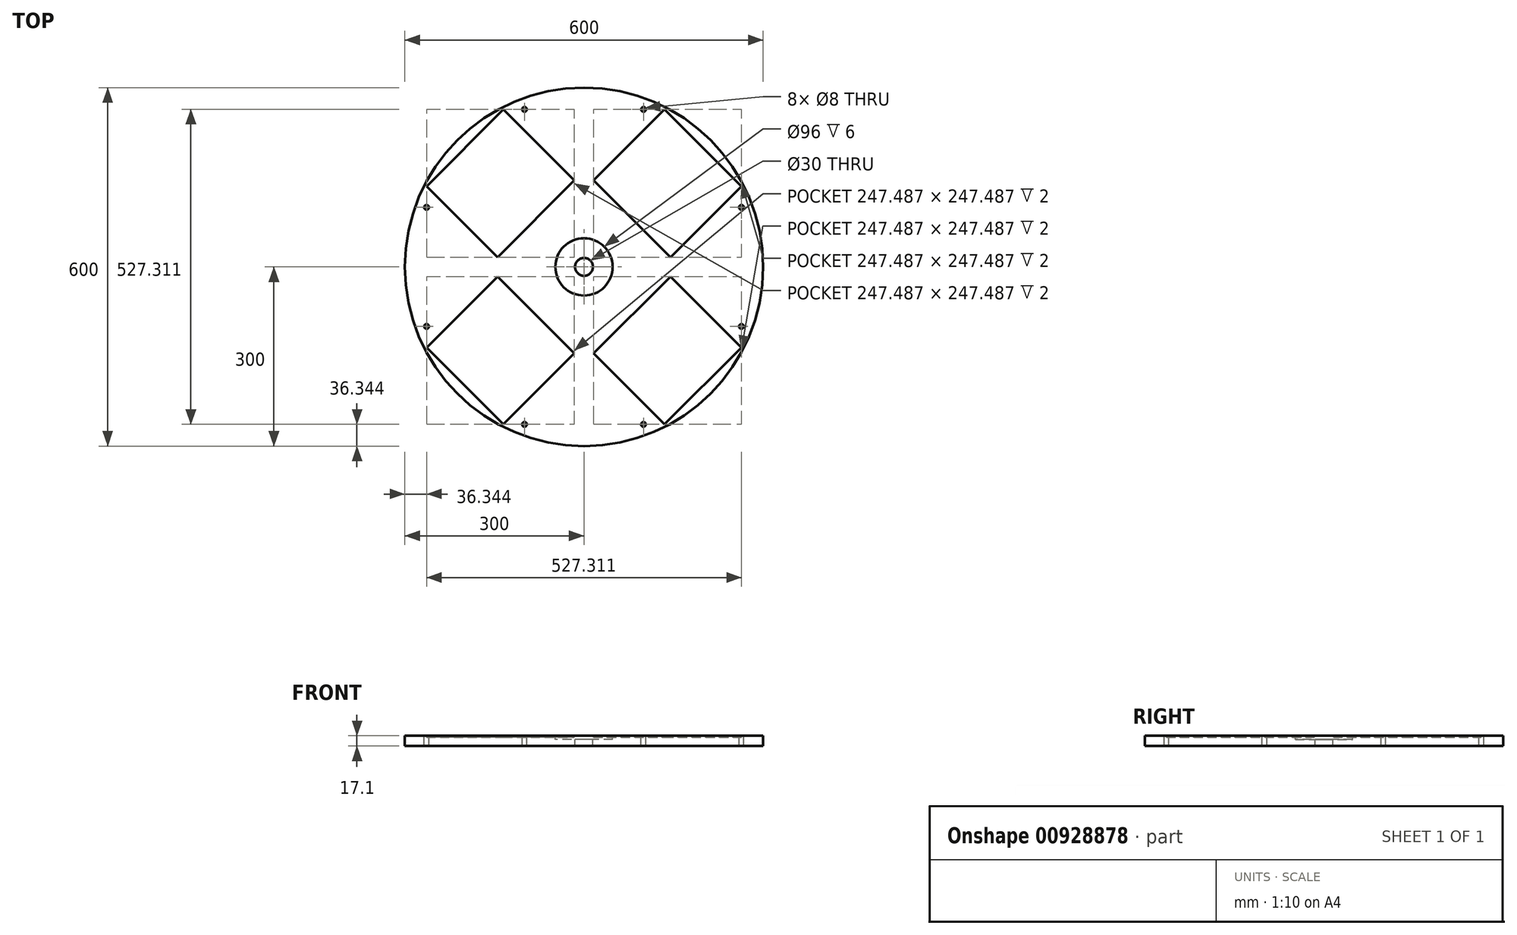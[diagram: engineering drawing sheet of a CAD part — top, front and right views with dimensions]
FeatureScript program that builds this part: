
annotation { "Feature Type Name" : "Feature", "Feature Type Description" : "" }
export const myFeature = defineFeature(function(context is Context, id is Id, definition is map)
    precondition{}
    {
        {
            var Q0;
            Q0=qCreatedBy(makeId("Top.planeOp"),FACE);
            var sketch = newSketch(context, id + "F0", { "sketchPlane" : qUnion([Q0])});
            skCircle(sketch, "E0", {"center": v(0, 0) * mm, "radius": 300 * mm});
            skSolve(sketch);
        }
        {
            var Q0;
            Q0=qSketchRegion(id+"F0",true);
            var Q1;
            Q1=makeQuery(id+"F0.imprint","IMPRINT",FACE,{"disambiguationData":[TD([[makeQuery(id+"F0.imprint","IMPRINT",EDGE,{"derivedFrom":sQuery(id+"F0.wireOp",EDGE,"AllwrVL7-AkE9-LfNM-VB61-ajPjN6t2vvd7.bottom")}),-1.0]])]});
            var Q2;
            Q2=makeQuery(id+"F0.imprint","IMPRINT",FACE,{"disambiguationData":[TD([[makeQuery(id+"F0.imprint","IMPRINT",EDGE,{"derivedFrom":sQuery(id+"F0.wireOp",EDGE,"5d97284d-aa32-4368-b48b-b87623f71f09.3.0")}),1.0]])]});
            var Q3;
            Q3=makeQuery(id+"F0.imprint","IMPRINT",FACE,{"disambiguationData":[TD([[makeQuery(id+"F0.imprint","IMPRINT",EDGE,{"derivedFrom":sQuery(id+"F0.wireOp",EDGE,"5d97284d-aa32-4368-b48b-b87623f71f09.2.0")}),1.0]])]});
            var Q4;
            Q4=makeQuery(id+"F0.imprint","IMPRINT",FACE,{"disambiguationData":[TD([[makeQuery(id+"F0.imprint","IMPRINT",EDGE,{"derivedFrom":sQuery(id+"F0.wireOp",EDGE,"5d97284d-aa32-4368-b48b-b87623f71f09.1.0")}),1.0]])]});
            extrude(context, id + "F1", {"entities" : qUnion([Q0, Q1, Q2, Q3, Q4]), "depth" : 17.1 * mm, "offsetDistance" : 25 * mm});
        }
        {
            var Q0;
            Q0=makeQuery(id+"F1.opExtrude","CAP_FACE",FACE,{"disambiguationData":[OSD([sQuery(id+"F0.wireOp",EDGE,"E0"),sQuery(id+"F0.wireOp",EDGE,"m1Yok3GX-FKcm-f6FL-vg4J-QwZKevZHBzbs.bottom"),sQuery(id+"F0.wireOp",EDGE,"m1Yok3GX-FKcm-f6FL-vg4J-QwZKevZHBzbs.top"),sQuery(id+"F0.wireOp",EDGE,"m1Yok3GX-FKcm-f6FL-vg4J-QwZKevZHBzbs.left"),sQuery(id+"F0.wireOp",EDGE,"m1Yok3GX-FKcm-f6FL-vg4J-QwZKevZHBzbs.right"),sQuery(id+"F0.wireOp",EDGE,"c3f3dfe4-16c6-495d-901e-fd32c168dcf2.1.0"),sQuery(id+"F0.wireOp",EDGE,"c3f3dfe4-16c6-495d-901e-fd32c168dcf2.1.1"),sQuery(id+"F0.wireOp",EDGE,"c3f3dfe4-16c6-495d-901e-fd32c168dcf2.1.2"),sQuery(id+"F0.wireOp",EDGE,"c3f3dfe4-16c6-495d-901e-fd32c168dcf2.1.3"),sQuery(id+"F0.wireOp",EDGE,"c3f3dfe4-16c6-495d-901e-fd32c168dcf2.2.0"),sQuery(id+"F0.wireOp",EDGE,"c3f3dfe4-16c6-495d-901e-fd32c168dcf2.2.1"),sQuery(id+"F0.wireOp",EDGE,"c3f3dfe4-16c6-495d-901e-fd32c168dcf2.2.2"),sQuery(id+"F0.wireOp",EDGE,"c3f3dfe4-16c6-495d-901e-fd32c168dcf2.2.3"),sQuery(id+"F0.wireOp",EDGE,"c3f3dfe4-16c6-495d-901e-fd32c168dcf2.3.0"),sQuery(id+"F0.wireOp",EDGE,"c3f3dfe4-16c6-495d-901e-fd32c168dcf2.3.1"),sQuery(id+"F0.wireOp",EDGE,"c3f3dfe4-16c6-495d-901e-fd32c168dcf2.3.2"),sQuery(id+"F0.wireOp",EDGE,"c3f3dfe4-16c6-495d-901e-fd32c168dcf2.3.3"),sQuery(id+"F0.wireOp",EDGE,"GgWlmIyM-ttYd-3ydM-N6fe-A3lpZPIy1D6L"),sQuery(id+"F0.wireOp",EDGE,"be6c052b-b5ba-4b0f-ad13-1682f92d27ab0.MirrorC"),sQuery(id+"F0.wireOp",EDGE,"65b34546-e90f-493b-8633-af6543c614b7.1.0"),sQuery(id+"F0.wireOp",EDGE,"65b34546-e90f-493b-8633-af6543c614b7.1.1"),sQuery(id+"F0.wireOp",EDGE,"65b34546-e90f-493b-8633-af6543c614b7.2.0"),sQuery(id+"F0.wireOp",EDGE,"65b34546-e90f-493b-8633-af6543c614b7.2.1"),sQuery(id+"F0.wireOp",EDGE,"65b34546-e90f-493b-8633-af6543c614b7.3.0"),sQuery(id+"F0.wireOp",EDGE,"65b34546-e90f-493b-8633-af6543c614b7.3.1"),sQuery(id+"F0.wireOp",EDGE,"Zrx7hTxE-zzg4-Czgn-36LA-upzHOa7QcTNY"),sQuery(id+"F0.wireOp",EDGE,"a1d9c7c6-3c1d-4fec-942b-8c6368d16cfa0.MirrorC"),sQuery(id+"F0.wireOp",EDGE,"64f4d127-5a3c-484e-af48-e4f96c13fd4a.1.0"),sQuery(id+"F0.wireOp",EDGE,"64f4d127-5a3c-484e-af48-e4f96c13fd4a.1.1"),sQuery(id+"F0.wireOp",EDGE,"64f4d127-5a3c-484e-af48-e4f96c13fd4a.2.0"),sQuery(id+"F0.wireOp",EDGE,"64f4d127-5a3c-484e-af48-e4f96c13fd4a.2.1"),sQuery(id+"F0.wireOp",EDGE,"64f4d127-5a3c-484e-af48-e4f96c13fd4a.3.0"),sQuery(id+"F0.wireOp",EDGE,"64f4d127-5a3c-484e-af48-e4f96c13fd4a.3.1")])],"isStart":false});
            var sketch = newSketch(context, id + "F2", { "sketchPlane" : qUnion([Q0])});
            skLineSegment(sketch, "E1", {"start": v(0, 0) * mm, "end": v(-212.13, -212.13) * mm, "construction": true});
            skLineSegment(sketch, "E2", {"start": v(0, 0) * mm, "end": v(-300, 0) * mm, "construction": true});
            skLineSegment(sketch, "E3", {"start": v(-263.66, -134.96) * mm, "end": v(-134.96, -263.66) * mm});
            skLineSegment(sketch, "E4", {"start": v(-134.96, -263.66) * mm, "end": v(-16.17, -144.86) * mm});
            skLineSegment(sketch, "E5", {"start": v(-16.17, -144.86) * mm, "end": v(-144.86, -16.17) * mm});
            skLineSegment(sketch, "E6", {"start": v(-144.86, -16.17) * mm, "end": v(-263.66, -134.96) * mm});
            skPoint(sketch, "E7", {"position": v(-199.3, -199.3) * mm});
            skLineSegment(sketch, "E8", {"start": v(0, 0) * mm, "end": v(212.13, 212.13) * mm, "construction": true});
            skLineSegment(sketch, "E9", {"start": v(0, 0) * mm, "end": v(212.13, -212.13) * mm, "construction": true});
            skLineSegment(sketch, "E10", {"start": v(-263.66, -134.96) * mm, "end": v(-266.48, -137.8) * mm});
            skLineSegment(sketch, "E11.1.0", {"start": v(16.17, -144.86) * mm, "end": v(134.96, -263.66) * mm});
            skLineSegment(sketch, "E11.1.1", {"start": v(144.86, -16.17) * mm, "end": v(16.17, -144.86) * mm});
            skLineSegment(sketch, "E11.1.2", {"start": v(263.66, -134.96) * mm, "end": v(144.86, -16.17) * mm});
            skLineSegment(sketch, "E11.1.3", {"start": v(134.96, -263.66) * mm, "end": v(263.66, -134.96) * mm});
            skLineSegment(sketch, "E11.2.0", {"start": v(144.86, 16.17) * mm, "end": v(263.66, 134.96) * mm});
            skLineSegment(sketch, "E11.2.1", {"start": v(16.17, 144.86) * mm, "end": v(144.86, 16.17) * mm});
            skLineSegment(sketch, "E11.2.2", {"start": v(134.96, 263.66) * mm, "end": v(16.17, 144.86) * mm});
            skLineSegment(sketch, "E11.2.3", {"start": v(263.66, 134.96) * mm, "end": v(134.96, 263.66) * mm});
            skLineSegment(sketch, "E11.3.0", {"start": v(-16.17, 144.86) * mm, "end": v(-134.96, 263.66) * mm});
            skLineSegment(sketch, "E11.3.1", {"start": v(-144.86, 16.17) * mm, "end": v(-16.17, 144.86) * mm});
            skLineSegment(sketch, "E11.3.2", {"start": v(-263.66, 134.96) * mm, "end": v(-144.86, 16.17) * mm});
            skLineSegment(sketch, "E11.3.3", {"start": v(-134.96, 263.66) * mm, "end": v(-263.66, 134.96) * mm});
            skPoint(sketch, "E11.center", {"position": v(0, 0) * mm});
            skSolve(sketch);
        }
        {
            var Q0;
            Q0=qSketchRegion(id+"F2",true);
            extrude(context, id + "F3", {"entities" : qUnion([Q0]), "operationType" : NewBodyOperationType.REMOVE, "oppositeDirection" : true, "depth" : 2 * mm, "offsetDistance" : 25 * mm});
        }
        {
            var Q0;
            Q0=makeQuery(id+"F1.opExtrude","CAP_FACE",FACE,{"disambiguationData":[OSD([sQuery(id+"F0.wireOp",EDGE,"E0"),sQuery(id+"F0.wireOp",EDGE,"m1Yok3GX-FKcm-f6FL-vg4J-QwZKevZHBzbs.bottom"),sQuery(id+"F0.wireOp",EDGE,"m1Yok3GX-FKcm-f6FL-vg4J-QwZKevZHBzbs.top"),sQuery(id+"F0.wireOp",EDGE,"m1Yok3GX-FKcm-f6FL-vg4J-QwZKevZHBzbs.left"),sQuery(id+"F0.wireOp",EDGE,"m1Yok3GX-FKcm-f6FL-vg4J-QwZKevZHBzbs.right"),sQuery(id+"F0.wireOp",EDGE,"c3f3dfe4-16c6-495d-901e-fd32c168dcf2.1.0"),sQuery(id+"F0.wireOp",EDGE,"c3f3dfe4-16c6-495d-901e-fd32c168dcf2.1.1"),sQuery(id+"F0.wireOp",EDGE,"c3f3dfe4-16c6-495d-901e-fd32c168dcf2.1.2"),sQuery(id+"F0.wireOp",EDGE,"c3f3dfe4-16c6-495d-901e-fd32c168dcf2.1.3"),sQuery(id+"F0.wireOp",EDGE,"c3f3dfe4-16c6-495d-901e-fd32c168dcf2.2.0"),sQuery(id+"F0.wireOp",EDGE,"c3f3dfe4-16c6-495d-901e-fd32c168dcf2.2.1"),sQuery(id+"F0.wireOp",EDGE,"c3f3dfe4-16c6-495d-901e-fd32c168dcf2.2.2"),sQuery(id+"F0.wireOp",EDGE,"c3f3dfe4-16c6-495d-901e-fd32c168dcf2.2.3"),sQuery(id+"F0.wireOp",EDGE,"c3f3dfe4-16c6-495d-901e-fd32c168dcf2.3.0"),sQuery(id+"F0.wireOp",EDGE,"c3f3dfe4-16c6-495d-901e-fd32c168dcf2.3.1"),sQuery(id+"F0.wireOp",EDGE,"c3f3dfe4-16c6-495d-901e-fd32c168dcf2.3.2"),sQuery(id+"F0.wireOp",EDGE,"c3f3dfe4-16c6-495d-901e-fd32c168dcf2.3.3"),sQuery(id+"F0.wireOp",EDGE,"GgWlmIyM-ttYd-3ydM-N6fe-A3lpZPIy1D6L"),sQuery(id+"F0.wireOp",EDGE,"be6c052b-b5ba-4b0f-ad13-1682f92d27ab0.MirrorC"),sQuery(id+"F0.wireOp",EDGE,"65b34546-e90f-493b-8633-af6543c614b7.1.0"),sQuery(id+"F0.wireOp",EDGE,"65b34546-e90f-493b-8633-af6543c614b7.1.1"),sQuery(id+"F0.wireOp",EDGE,"65b34546-e90f-493b-8633-af6543c614b7.2.0"),sQuery(id+"F0.wireOp",EDGE,"65b34546-e90f-493b-8633-af6543c614b7.2.1"),sQuery(id+"F0.wireOp",EDGE,"65b34546-e90f-493b-8633-af6543c614b7.3.0"),sQuery(id+"F0.wireOp",EDGE,"65b34546-e90f-493b-8633-af6543c614b7.3.1"),sQuery(id+"F0.wireOp",EDGE,"Zrx7hTxE-zzg4-Czgn-36LA-upzHOa7QcTNY"),sQuery(id+"F0.wireOp",EDGE,"a1d9c7c6-3c1d-4fec-942b-8c6368d16cfa0.MirrorC"),sQuery(id+"F0.wireOp",EDGE,"64f4d127-5a3c-484e-af48-e4f96c13fd4a.1.0"),sQuery(id+"F0.wireOp",EDGE,"64f4d127-5a3c-484e-af48-e4f96c13fd4a.1.1"),sQuery(id+"F0.wireOp",EDGE,"64f4d127-5a3c-484e-af48-e4f96c13fd4a.2.0"),sQuery(id+"F0.wireOp",EDGE,"64f4d127-5a3c-484e-af48-e4f96c13fd4a.2.1"),sQuery(id+"F0.wireOp",EDGE,"64f4d127-5a3c-484e-af48-e4f96c13fd4a.3.0"),sQuery(id+"F0.wireOp",EDGE,"64f4d127-5a3c-484e-af48-e4f96c13fd4a.3.1"),sQuery(id+"F0.wireOp",EDGE,"AllwrVL7-AkE9-LfNM-VB61-ajPjN6t2vvd7.bottom"),sQuery(id+"F0.wireOp",EDGE,"AllwrVL7-AkE9-LfNM-VB61-ajPjN6t2vvd7.top"),sQuery(id+"F0.wireOp",EDGE,"AllwrVL7-AkE9-LfNM-VB61-ajPjN6t2vvd7.left"),sQuery(id+"F0.wireOp",EDGE,"AllwrVL7-AkE9-LfNM-VB61-ajPjN6t2vvd7.right"),sQuery(id+"F0.wireOp",EDGE,"vhIM6kYj-bil8-T5aC-Hw9W-HzG7wACOchpu.bottom"),sQuery(id+"F0.wireOp",EDGE,"vhIM6kYj-bil8-T5aC-Hw9W-HzG7wACOchpu.top"),sQuery(id+"F0.wireOp",EDGE,"vhIM6kYj-bil8-T5aC-Hw9W-HzG7wACOchpu.left"),sQuery(id+"F0.wireOp",EDGE,"vhIM6kYj-bil8-T5aC-Hw9W-HzG7wACOchpu.right"),sQuery(id+"F0.wireOp",EDGE,"e5db2dc1-b70e-487e-85e1-c1db5f647828.1.0"),sQuery(id+"F0.wireOp",EDGE,"e5db2dc1-b70e-487e-85e1-c1db5f647828.1.1"),sQuery(id+"F0.wireOp",EDGE,"e5db2dc1-b70e-487e-85e1-c1db5f647828.1.2"),sQuery(id+"F0.wireOp",EDGE,"e5db2dc1-b70e-487e-85e1-c1db5f647828.1.3"),sQuery(id+"F0.wireOp",EDGE,"e5db2dc1-b70e-487e-85e1-c1db5f647828.1.4"),sQuery(id+"F0.wireOp",EDGE,"e5db2dc1-b70e-487e-85e1-c1db5f647828.1.5"),sQuery(id+"F0.wireOp",EDGE,"e5db2dc1-b70e-487e-85e1-c1db5f647828.1.6"),sQuery(id+"F0.wireOp",EDGE,"e5db2dc1-b70e-487e-85e1-c1db5f647828.1.7"),sQuery(id+"F0.wireOp",EDGE,"e5db2dc1-b70e-487e-85e1-c1db5f647828.2.0"),sQuery(id+"F0.wireOp",EDGE,"e5db2dc1-b70e-487e-85e1-c1db5f647828.2.1"),sQuery(id+"F0.wireOp",EDGE,"e5db2dc1-b70e-487e-85e1-c1db5f647828.2.2"),sQuery(id+"F0.wireOp",EDGE,"e5db2dc1-b70e-487e-85e1-c1db5f647828.2.3"),sQuery(id+"F0.wireOp",EDGE,"e5db2dc1-b70e-487e-85e1-c1db5f647828.2.4"),sQuery(id+"F0.wireOp",EDGE,"e5db2dc1-b70e-487e-85e1-c1db5f647828.2.5"),sQuery(id+"F0.wireOp",EDGE,"e5db2dc1-b70e-487e-85e1-c1db5f647828.2.6"),sQuery(id+"F0.wireOp",EDGE,"e5db2dc1-b70e-487e-85e1-c1db5f647828.2.7"),sQuery(id+"F0.wireOp",EDGE,"e5db2dc1-b70e-487e-85e1-c1db5f647828.3.0"),sQuery(id+"F0.wireOp",EDGE,"e5db2dc1-b70e-487e-85e1-c1db5f647828.3.1"),sQuery(id+"F0.wireOp",EDGE,"e5db2dc1-b70e-487e-85e1-c1db5f647828.3.2"),sQuery(id+"F0.wireOp",EDGE,"e5db2dc1-b70e-487e-85e1-c1db5f647828.3.3"),sQuery(id+"F0.wireOp",EDGE,"e5db2dc1-b70e-487e-85e1-c1db5f647828.3.4"),sQuery(id+"F0.wireOp",EDGE,"e5db2dc1-b70e-487e-85e1-c1db5f647828.3.5"),sQuery(id+"F0.wireOp",EDGE,"e5db2dc1-b70e-487e-85e1-c1db5f647828.3.6"),sQuery(id+"F0.wireOp",EDGE,"e5db2dc1-b70e-487e-85e1-c1db5f647828.3.7")])],"isStart":false});
            var sketch = newSketch(context, id + "F4", { "sketchPlane" : qUnion([Q0])});
            skLineSegment(sketch, "E12", {"start": v(-263.66, -99.6) * mm, "end": v(-245.98, -117.28) * mm, "construction": true});
            skCircle(sketch, "E13", {"center": v(-263.66, -99.6) * mm, "radius": 4 * mm});
            skLineSegment(sketch, "E14", {"start": v(-99.6, -263.66) * mm, "end": v(-117.28, -245.98) * mm, "construction": true});
            skCircle(sketch, "E15", {"center": v(-99.6, -263.66) * mm, "radius": 4 * mm});
            skCircle(sketch, "E16.1.0", {"center": v(99.6, -263.66) * mm, "radius": 4 * mm});
            skCircle(sketch, "E16.1.1", {"center": v(263.66, -99.6) * mm, "radius": 4 * mm});
            skCircle(sketch, "E16.2.0", {"center": v(263.66, 99.6) * mm, "radius": 4 * mm});
            skCircle(sketch, "E16.2.1", {"center": v(99.6, 263.66) * mm, "radius": 4 * mm});
            skCircle(sketch, "E16.3.0", {"center": v(-99.6, 263.66) * mm, "radius": 4 * mm});
            skCircle(sketch, "E16.3.1", {"center": v(-263.66, 99.6) * mm, "radius": 4 * mm});
            skPoint(sketch, "E16.center", {"position": v(0, 0) * mm});
            skSolve(sketch);
        }
        {
            var Q0;
            Q0=qSketchRegion(id+"F4",true);
            extrude(context, id + "F5", {"entities" : qUnion([Q0]), "operationType" : NewBodyOperationType.REMOVE, "oppositeDirection" : true, "depth" : 25 * mm, "offsetDistance" : 25 * mm});
        }
        {
            var Q0;
            Q0=makeQuery(id+"F1.opExtrude","CAP_FACE",FACE,{"disambiguationData":[OSD([sQuery(id+"F0.wireOp",EDGE,"E0")])],"isStart":false});
            var sketch = newSketch(context, id + "F6", { "sketchPlane" : qUnion([Q0])});
            skCircle(sketch, "E17", {"center": v(0, 0) * mm, "radius": 48 * mm});
            skSolve(sketch);
        }
        {
            var Q0;
            Q0=makeQuery(id+"F6.imprint","IMPRINT",FACE,{"disambiguationData":[TD([[makeQuery(id+"F6.imprint","IMPRINT",EDGE,{"derivedFrom":sQuery(id+"F6.wireOp",EDGE,"E17")}),1.0]])]});
            extrude(context, id + "F7", {"entities" : qUnion([Q0]), "operationType" : NewBodyOperationType.REMOVE, "oppositeDirection" : true, "depth" : 6 * mm, "offsetDistance" : 25 * mm});
        }
        {
            var Q0;
            Q0=makeQuery(id+"F7.boolean.opBoolean","COPY",FACE,{"derivedFrom":makeQuery(id+"F7.opExtrude","CAP_FACE",FACE,{"disambiguationData":[OSD([sQuery(id+"F6.wireOp",EDGE,"E17")])],"isStart":false})});
            var sketch = newSketch(context, id + "F8", { "sketchPlane" : qUnion([Q0])});
            skCircle(sketch, "E18", {"center": v(0, 0) * mm, "radius": 15 * mm});
            skSolve(sketch);
        }
        {
            var Q0;
            Q0=makeQuery(id+"F8.imprint","IMPRINT",FACE,{"disambiguationData":[TD([[makeQuery(id+"F8.imprint","IMPRINT",EDGE,{"derivedFrom":sQuery(id+"F8.wireOp",EDGE,"E18")}),1.0]])]});
            extrude(context, id + "F9", {"entities" : qUnion([Q0]), "operationType" : NewBodyOperationType.REMOVE, "endBound" : BoundingType.THROUGH_ALL, "oppositeDirection" : true, "depth" : 25 * mm, "offsetDistance" : 25 * mm});
        }
    });
